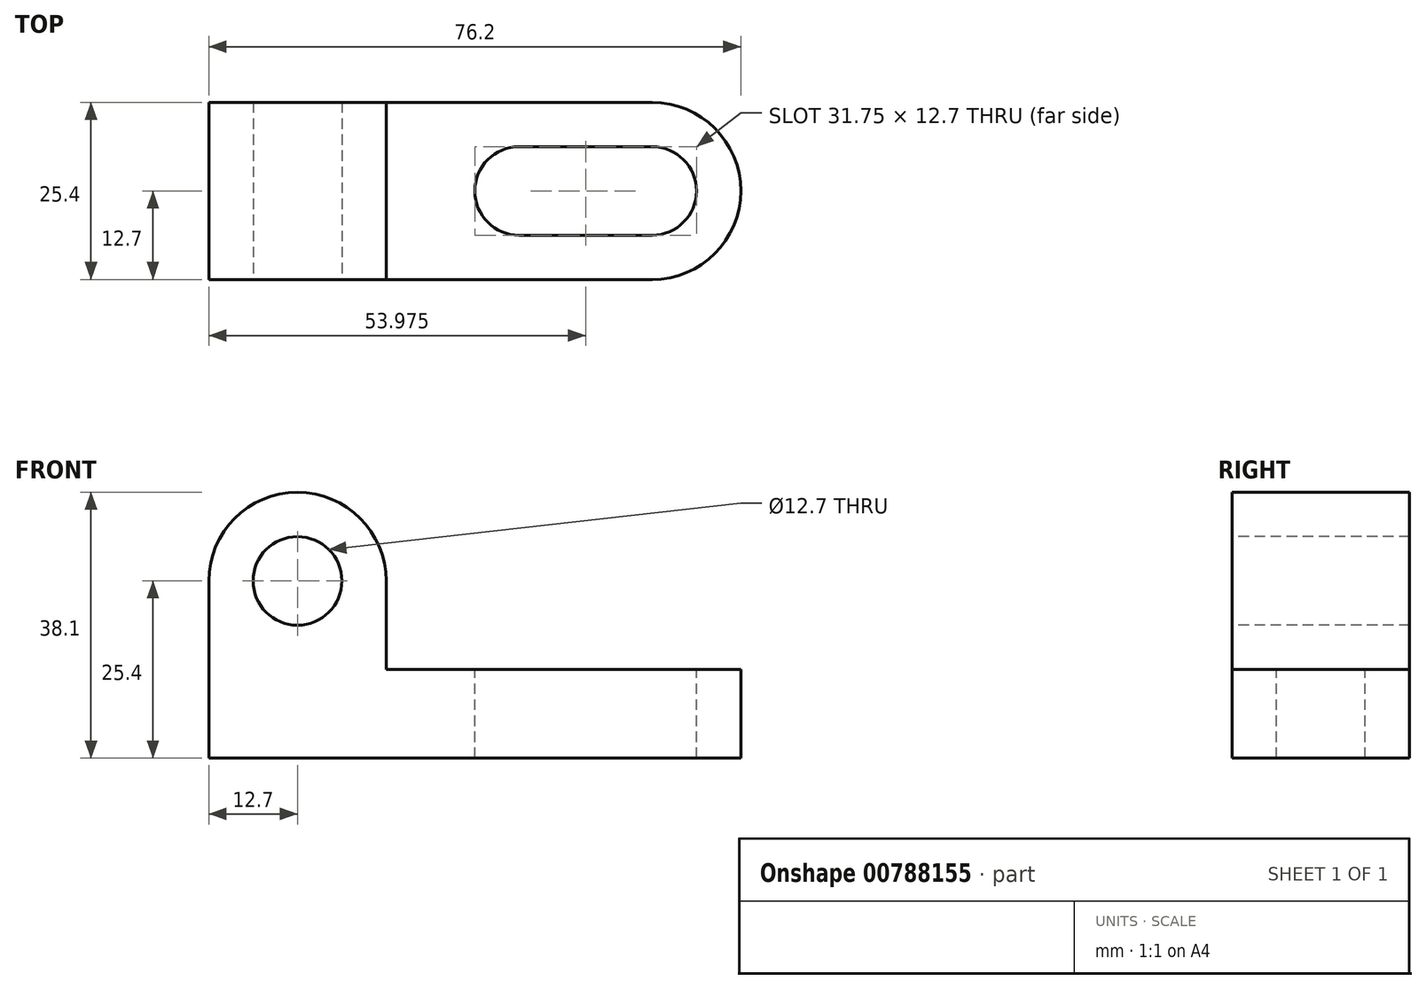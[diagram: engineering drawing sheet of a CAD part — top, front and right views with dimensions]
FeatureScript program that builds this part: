
annotation { "Feature Type Name" : "Feature", "Feature Type Description" : "" }
export const myFeature = defineFeature(function(context is Context, id is Id, definition is map)
    precondition{}
    {
        {
            var Q0;
            Q0=qCreatedBy(makeId("Front.planeOp"),FACE);
            var sketch = newSketch(context, id + "F0", { "sketchPlane" : qUnion([Q0])});
            skLineSegment(sketch, "E0", {"start": v(0, 0) * mm, "end": v(76.2, 0) * mm});
            skLineSegment(sketch, "E1", {"start": v(76.2, 12.7) * mm, "end": v(25.4, 12.7) * mm});
            skLineSegment(sketch, "E2", {"start": v(25.4, 12.7) * mm, "end": v(25.4, 38.1) * mm});
            skLineSegment(sketch, "E3", {"start": v(25.4, 38.1) * mm, "end": v(0, 38.1) * mm});
            skLineSegment(sketch, "E4", {"start": v(0, 38.1) * mm, "end": v(0, 0) * mm});
            skLineSegment(sketch, "E5", {"start": v(76.2, 12.7) * mm, "end": v(76.2, 0) * mm});
            skSolve(sketch);
        }
        {
            var Q0;
            Q0=makeQuery(id+"F0.imprint","IMPRINT",FACE,{"disambiguationData":[TD([[makeQuery(id+"F0.imprint","IMPRINT",EDGE,{"derivedFrom":sQuery(id+"F0.wireOp",EDGE,"E0")}),1.0]])]});
            extrude(context, id + "F1", {"entities" : qUnion([Q0]), "depth" : 25.4 * mm, "offsetDistance" : 25.4 * mm});
        }
        {
            var Q0;
            Q0=makeQuery(id+"F1.opExtrude","SWEPT_EDGE",EDGE,{"disambiguationData":[OSD([sQuery(id+"F0.wireOp",EDGE,"E2"),sQuery(id+"F0.wireOp",EDGE,"E3")])]});
            var Q1;
            Q1=makeQuery(id+"F1.opExtrude","SWEPT_EDGE",EDGE,{"disambiguationData":[OSD([sQuery(id+"F0.wireOp",EDGE,"E3"),sQuery(id+"F0.wireOp",EDGE,"E4")])]});
            var Q2;
            Q2=makeQuery(id+"F1.opExtrude","CAP_EDGE",EDGE,{"disambiguationData":[OSD([sQuery(id+"F0.wireOp",EDGE,"E5")])],"isStart":false});
            var Q3;
            Q3=makeQuery(id+"F1.opExtrude","CAP_EDGE",EDGE,{"disambiguationData":[OSD([sQuery(id+"F0.wireOp",EDGE,"E5")])],"isStart":true});
            fillet(context, id + "F2", {"entities" : qUnion([Q0, Q1, Q2, Q3]), "radius" : 12.7 * mm, "tangentPropagation" : true, "allowEdgeOverflow" : false});
        }
        {
            var Q0;
            Q0=makeQuery(id+"F1.opExtrude","CAP_FACE",FACE,{"disambiguationData":[OSD([sQuery(id+"F0.wireOp",EDGE,"E0"),sQuery(id+"F0.wireOp",EDGE,"E1"),sQuery(id+"F0.wireOp",EDGE,"E2"),sQuery(id+"F0.wireOp",EDGE,"E3"),sQuery(id+"F0.wireOp",EDGE,"E4"),sQuery(id+"F0.wireOp",EDGE,"E5")])],"isStart":false});
            var sketch = newSketch(context, id + "F3", { "sketchPlane" : qUnion([Q0])});
            skCircle(sketch, "E6", {"center": v(12.7, 25.4) * mm, "radius": 6.35 * mm});
            skSolve(sketch);
        }
        {
            var Q0;
            Q0=makeQuery(id+"F3.imprint","IMPRINT",FACE,{"disambiguationData":[TD([[makeQuery(id+"F3.imprint","IMPRINT",EDGE,{"derivedFrom":sQuery(id+"F3.wireOp",EDGE,"E6")}),1.0]])]});
            extrude(context, id + "F4", {"entities" : qUnion([Q0]), "operationType" : NewBodyOperationType.REMOVE, "oppositeDirection" : true, "depth" : 25.4 * mm, "offsetDistance" : 25.4 * mm});
        }
        {
            var Q0;
            Q0=makeQuery(id+"F1.opExtrude","SWEPT_FACE",FACE,{"disambiguationData":[OSD([sQuery(id+"F0.wireOp",EDGE,"E1")])]});
            var sketch = newSketch(context, id + "F5", { "sketchPlane" : qUnion([Q0])});
            skCircle(sketch, "E7", {"center": v(44.45, -12.7) * mm, "radius": 6.35 * mm});
            skCircle(sketch, "E8", {"center": v(63.5, -12.7) * mm, "radius": 6.35 * mm});
            skLineSegment(sketch, "E9", {"start": v(44.45, -6.35) * mm, "end": v(63.5, -6.35) * mm});
            skLineSegment(sketch, "E10", {"start": v(44.45, -19.05) * mm, "end": v(63.5, -19.05) * mm});
            skPoint(sketch, "E10.startSnap0", {"position": v(44.45, -25.4) * mm});
            skSolve(sketch);
        }
        {
            var Q0;
            {var subQ0=sQuery(id+"F5.wireOp",EDGE,"E7");var subQ1=makeQuery(id+"F5.imprint","INTERSECT",VERTEX,{"derivedFrom":[subQ0,sQuery(id+"F5.wireOp",EDGE,"E9")]});Q0=makeQuery(id+"F5.imprint","IMPRINT",FACE,{"disambiguationData":[TD([[makeQuery(id+"F5.imprint","IMPRINT",EDGE,{"disambiguationData":[TD([[subQ1,-1.0]])],"derivedFrom":subQ0}),1.0]])]});}
            var Q1;
            {var subQ0=sQuery(id+"F5.wireOp",EDGE,"E9");Q1=makeQuery(id+"F5.imprint","IMPRINT",FACE,{"disambiguationData":[TD([[makeQuery(id+"F5.imprint","IMPRINT",EDGE,{"derivedFrom":subQ0}),-1.0]])]});}
            var Q2;
            {var subQ0=sQuery(id+"F5.wireOp",EDGE,"E8");var subQ1=makeQuery(id+"F5.imprint","INTERSECT",VERTEX,{"derivedFrom":[subQ0,sQuery(id+"F5.wireOp",EDGE,"E9")]});Q2=makeQuery(id+"F5.imprint","IMPRINT",FACE,{"disambiguationData":[TD([[makeQuery(id+"F5.imprint","IMPRINT",EDGE,{"disambiguationData":[TD([[subQ1,-1.0]])],"derivedFrom":subQ0}),1.0]])]});}
            extrude(context, id + "F6", {"entities" : qUnion([Q0, Q1, Q2]), "operationType" : NewBodyOperationType.REMOVE, "oppositeDirection" : true, "depth" : 25.4 * mm, "offsetDistance" : 25.4 * mm});
        }
    });
